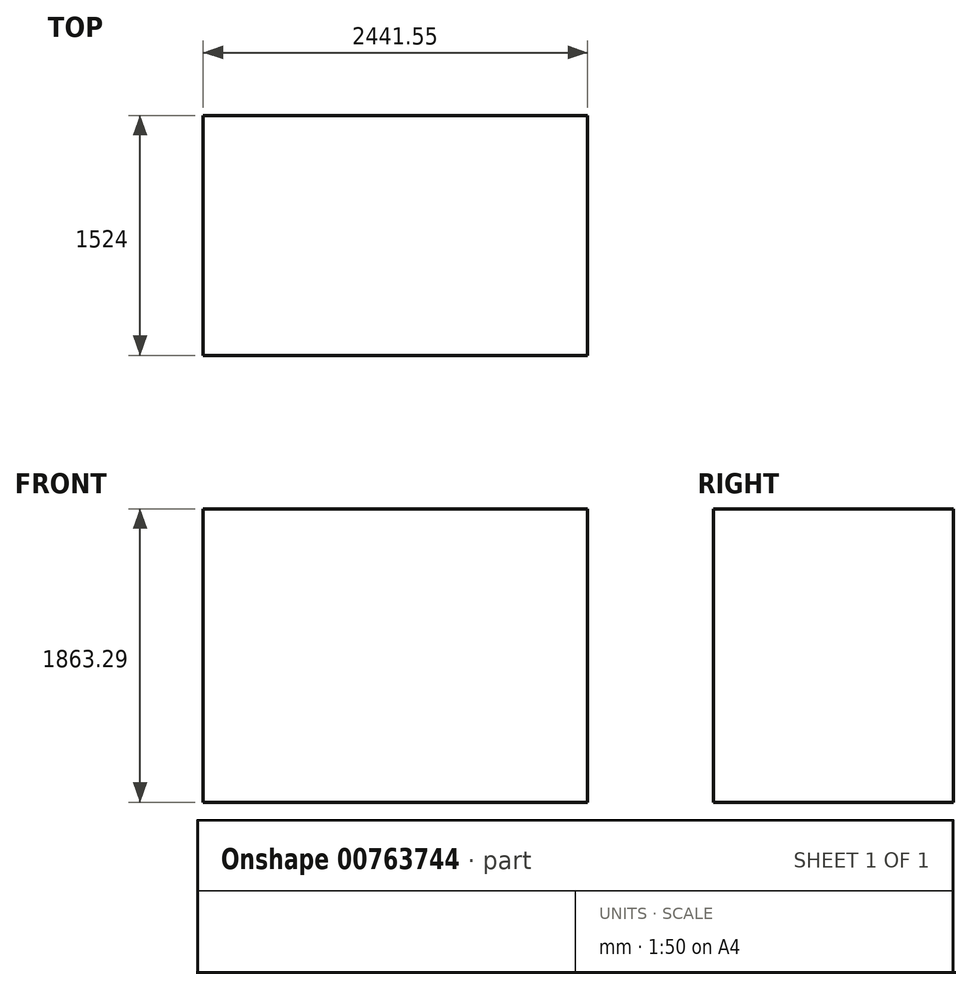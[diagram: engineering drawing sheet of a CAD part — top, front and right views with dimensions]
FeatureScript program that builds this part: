
annotation { "Feature Type Name" : "Feature", "Feature Type Description" : "" }
export const myFeature = defineFeature(function(context is Context, id is Id, definition is map)
    precondition{}
    {
        {
            var Q0;
            Q0=qCreatedBy(makeId("Front.planeOp"),FACE);
            var sketch = newSketch(context, id + "F0", { "sketchPlane" : qUnion([Q0])});
            skLineSegment(sketch, "E0.bottom", {"start": v(0, 0) * mm, "end": v(7620, 0) * mm, "construction": true});
            skLineSegment(sketch, "E0.top", {"start": v(0, -5080) * mm, "end": v(7620, -5080) * mm, "construction": true});
            skLineSegment(sketch, "E0.left", {"start": v(0, 0) * mm, "end": v(0, -5080) * mm, "construction": true});
            skLineSegment(sketch, "E0.right", {"start": v(7620, 0) * mm, "end": v(7620, -5080) * mm, "construction": true});
            skLineSegment(sketch, "E1.bottom", {"start": v(2842.1, -1787.57) * mm, "end": v(5283.66, -1787.57) * mm});
            skLineSegment(sketch, "E1.top", {"start": v(2842.1, -3650.86) * mm, "end": v(5283.66, -3650.86) * mm});
            skLineSegment(sketch, "E1.left", {"start": v(2842.1, -1787.57) * mm, "end": v(2842.1, -3650.86) * mm});
            skLineSegment(sketch, "E1.right", {"start": v(5283.66, -1787.57) * mm, "end": v(5283.66, -3650.86) * mm});
            skSolve(sketch);
        }
        {
            var Q0;
            Q0 = qSketchRegion(id + "F0", true);
            extrude(context, id + "F1", {"entities" : qUnion([Q0]), "depth" : 1524 * mm, "offsetDistance" : 25.4 * mm});
        }
    });
